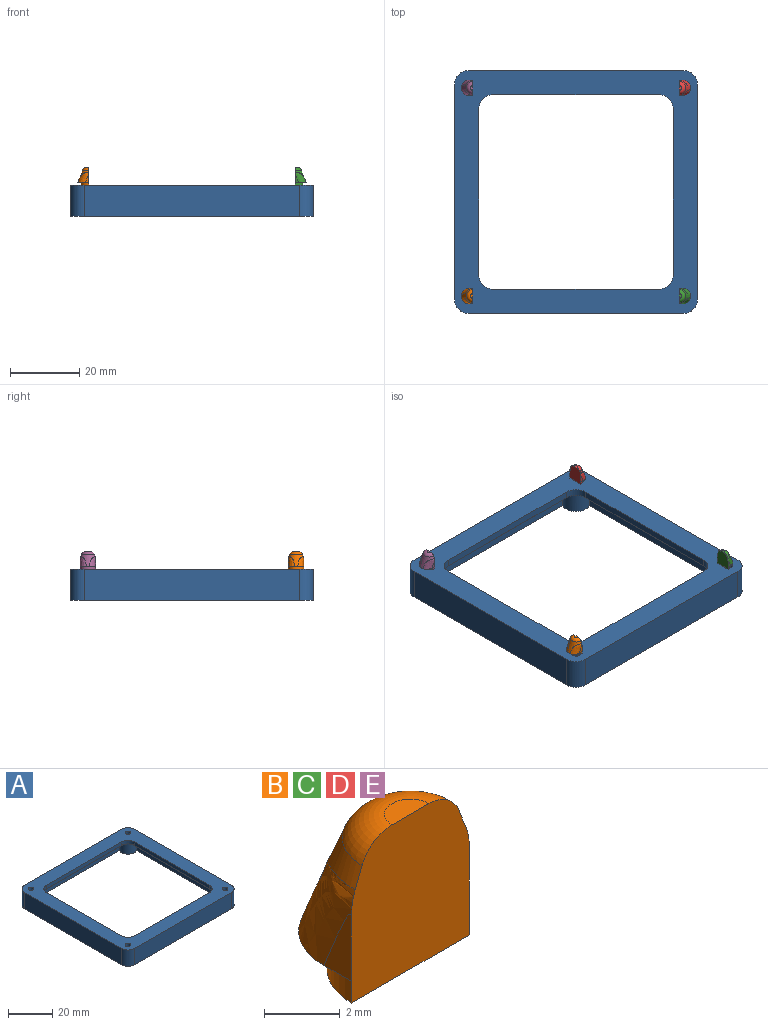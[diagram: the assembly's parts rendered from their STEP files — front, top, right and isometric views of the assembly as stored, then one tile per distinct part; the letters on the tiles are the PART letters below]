
ASSEMBLY  parts=5 mates=4
PART A: 38 faces, bbox 70x70x9 mm
  f0: plane 4x4mm, normal (0,0,-1), area 3.4mm2, adj f26,f36,f37
  f1: plane 4x4mm, normal (0,0,-1), area 3.4mm2, adj f27,f34,f36
  f2: plane 4x4mm, normal (0,0,-1), area 3.4mm2, adj f28,f34,f35
  f3: plane 48x2mm, normal (0,-1,0), area 96mm2, adj f8,f26,f29,f37
  f4: plane 48x2mm, normal (-1,0,0), area 96mm2, adj f8,f26,f27,f36
  f5: plane 48x2mm, normal (0,1,0), area 96mm2, adj f8,f27,f28,f34
  f6: plane 48x2mm, normal (1,0,0), area 96mm2, adj f8,f28,f29,f35
  f7: plane 4x4mm, normal (0,0,-1), area 3.4mm2, adj f29,f35,f37
  f8: plane 70x70mm, normal (0,0,1), area 1744.4mm2, adj f3,f4,f5,f6,f17,f18,f19,f20
  f9: plane 55.07x2mm, normal (0,1,0), area 110.1mm2, adj f13,f16,f25,f34
  f10: plane 55.07x2mm, normal (-1,0,0), area 110.1mm2, adj f15,f16,f25,f36
  f11: plane 55.07x2mm, normal (0,-1,0), area 110.1mm2, adj f14,f15,f25,f37
  f12: plane 55.07x2mm, normal (1,0,0), area 110.1mm2, adj f13,f14,f25,f35
  f13: cylinder r=4mm len=7mm, axis (0,0,1), area 61.9mm2, adj f9,f12,f25,f34,f35
  f14: cylinder r=4mm len=7mm, axis (0,0,1), area 61.9mm2, adj f11,f12,f25,f35,f37
  f15: cylinder r=4mm len=7mm, axis (0,0,1), area 61.9mm2, adj f10,f11,f25,f36,f37
  f16: cylinder r=4mm len=7mm, axis (0,0,1), area 61.9mm2, adj f9,f10,f25,f34,f36
  f17: cylinder r=4mm len=9mm, axis (0,0,1), area 56.5mm2, adj f8,f18,f24,f25
  f18: plane 62x9mm, normal (0,-1,0), area 558mm2, adj f8,f17,f19,f25
  f19: cylinder r=4mm len=9mm, axis (0,0,1), area 56.5mm2, adj f8,f18,f20,f25
  f20: plane 62x9mm, normal (1,0,0), area 558mm2, adj f8,f19,f21,f25
  f21: cylinder r=4mm len=9mm, axis (0,0,1), area 56.5mm2, adj f8,f20,f22,f25
  f22: plane 62x9mm, normal (0,1,0), area 558mm2, adj f8,f21,f23,f25
  f23: cylinder r=4mm len=9mm, axis (0,0,1), area 56.5mm2, adj f8,f22,f24,f25
  f24: plane 62x9mm, normal (-1,0,0), area 558mm2, adj f8,f17,f23,f25
  f25: plane 70x70mm, normal (0,0,-1), area 638.1mm2, adj f9,f10,f11,f12,f13,f14,f15,f16
  f26: cylinder r=4mm len=4mm, axis (0,0,-1), area 12.6mm2, adj f0,f3,f4,f8
  f27: cylinder r=4mm len=4mm, axis (0,0,1), area 12.6mm2, adj f1,f4,f5,f8
  f28: cylinder r=4mm len=4mm, axis (0,0,-1), area 12.6mm2, adj f2,f5,f6,f8
  f29: cylinder r=4mm len=4mm, axis (0,0,1), area 12.6mm2, adj f3,f6,f7,f8
  f30: cylinder r=1.25mm len=9mm, axis (0,0,1), area 70.7mm2, adj f8,f25
  f31: cylinder r=1.25mm len=9mm, axis (0,0,1), area 70.7mm2, adj f8,f25
  f32: cylinder r=1.25mm len=9mm, axis (0,0,1), area 70.7mm2, adj f8,f25
  f33: cylinder r=1.25mm len=9mm, axis (0,0,1), area 70.7mm2, adj f8,f25
  f34: cylinder r=5mm len=56.34mm, axis (-1,0,0), area 429.1mm2, adj f1,f2,f5,f9,f13,f16,f35,f36
  f35: cylinder r=5mm len=56.34mm, axis (0,1,0), area 429.1mm2, adj f2,f6,f7,f12,f13,f14,f34,f37
  f36: cylinder r=5mm len=56.34mm, axis (0,-1,0), area 429.1mm2, adj f0,f1,f4,f10,f15,f16,f34,f37
  f37: cylinder r=5mm len=56.34mm, axis (1,0,0), area 429.1mm2, adj f0,f3,f7,f11,f14,f15,f35,f36
PART B: 11 faces, bbox 6.7x3.8x5.8 mm
  f0: cone r=1.8mm half-angle=21.6deg, axis (0,0,-1), area 9.7mm2, adj f1,f2,f6,f9,f10
  f1: plane 4.65x3.45mm, normal (0,0,-1), area 4.6mm2, adj f0,f3,f7,f8,f9,f10
  f2: plane 5x4.4mm, normal (0,-1,0), area 20.5mm2, adj f0,f3,f4,f5,f6,f7,f8,f9
  f3: cylinder r=2.2mm len=4.4mm, axis (0,0,1), area 4.8mm2, adj f1,f2,f4
  f4: plane 4.4x2.2mm, normal (0,0,-1), area 7.6mm2, adj f2,f3
  f5: plane 1.37x0.68mm, normal (0,0,1), area 0.7mm2, adj f2,f6
  f6: torus R=0.68mm, axis (0,0,1), area 5.9mm2, adj f0,f2,f5
  f7: plane 2.15x1.03mm, normal (1,0,0), area 1.2mm2, adj f1,f2,f10
  f8: plane 2.15x1.03mm, normal (-1,0,0), area 1.2mm2, adj f1,f2,f9
  f9: bspline ~4.14x3.56mm, area 7.5mm2, adj f0,f1,f2,f8
  f10: bspline ~4.14x3.56mm, area 7.5mm2, adj f0,f1,f2,f7
PART C: same geometry as B
PART D: same geometry as B
PART E: same geometry as B
PLACE A at identity
PLACE B rot(axis=(0,0,1),90deg) t=(-29.75,-30,0)mm
PLACE C rot(axis=(0,0,-1),90deg) t=(29.75,-30,0)mm
PLACE D rot(axis=(0,0,-1),90deg) t=(29.75,30,0)mm
PLACE E rot(axis=(0,0,1),90deg) t=(-29.75,30,0)mm
MATE fastened B.f3 <-> A.f8  axis (0,0,-1) through (-29.75,-30,0)mm
MATE fastened C.f3 <-> A.f8  axis (0,0,-1) through (29.75,-30,0)mm
MATE fastened D.f3 <-> A.f8  axis (0,0,-1) through (29.75,30,0)mm
MATE fastened E.f3 <-> A.f8  axis (0,0,-1) through (-29.75,30,0)mm
